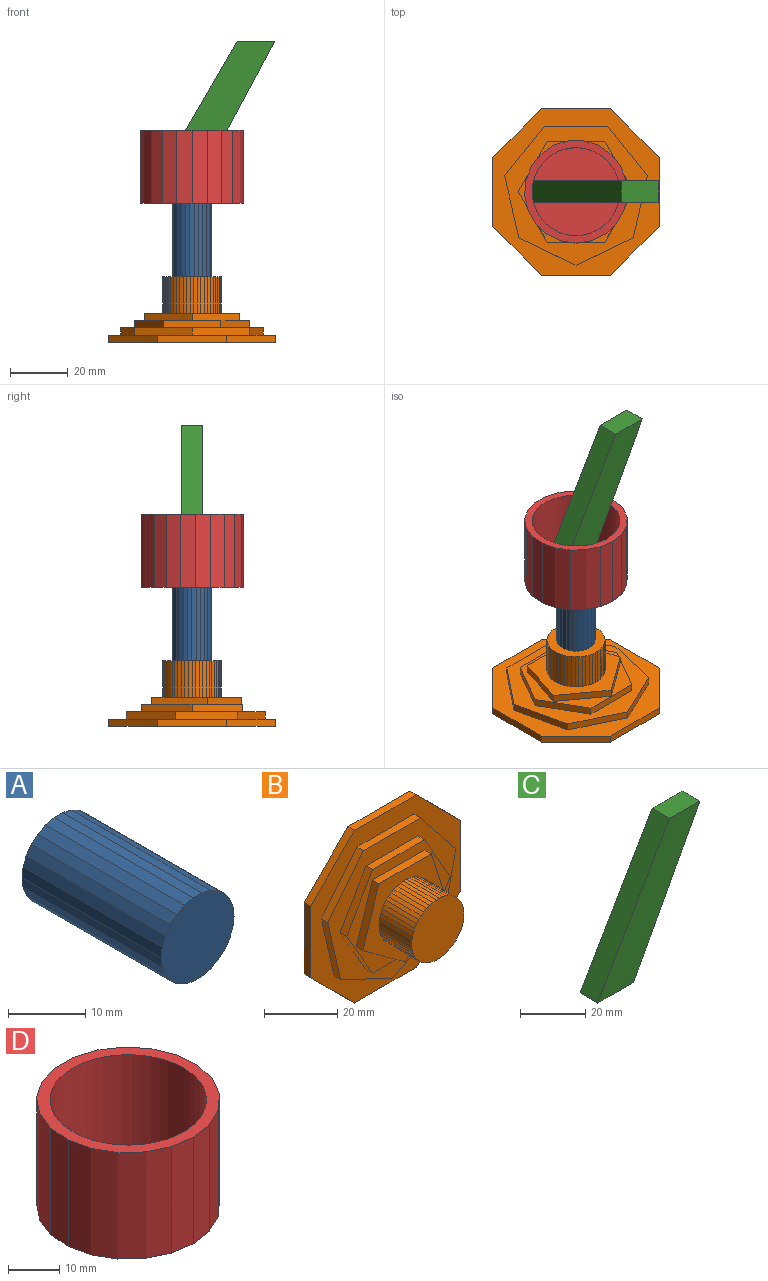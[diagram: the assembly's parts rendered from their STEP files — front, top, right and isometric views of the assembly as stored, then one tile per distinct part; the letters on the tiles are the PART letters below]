
ASSEMBLY  parts=4 mates=3
PART A: 28 faces, bbox 13.3x25.4x13.2 mm
  f0: plane 25.4x1.6mm, normal (0,0,-1), area 40.7mm2, adj f1,f25,f26,f27
  f1: plane 25.4x1.56mm, normal (0.24,0,-0.97), area 40.7mm2, adj f0,f2,f26,f27
  f2: plane 25.4x1.42mm, normal (0.46,0,-0.89), area 40.7mm2, adj f1,f3,f26,f27
  f3: plane 25.4x1.2mm, normal (0.66,0,-0.75), area 40.7mm2, adj f2,f4,f26,f27
  f4: plane 25.4x1.32mm, normal (0.82,0,-0.57), area 40.7mm2, adj f3,f5,f26,f27
  f5: plane 25.4x1.5mm, normal (0.94,0,-0.35), area 40.7mm2, adj f4,f6,f26,f27
  f6: plane 25.4x1.59mm, normal (0.99,0,-0.12), area 40.7mm2, adj f5,f7,f26,f27
  f7: plane 25.4x1.59mm, normal (0.99,0,0.12), area 40.7mm2, adj f6,f8,f26,f27
  f8: plane 25.4x1.5mm, normal (0.94,0,0.35), area 40.7mm2, adj f7,f9,f26,f27
  f9: plane 25.4x1.32mm, normal (0.82,0,0.57), area 40.7mm2, adj f8,f10,f26,f27
  f10: plane 25.4x1.2mm, normal (0.66,0,0.75), area 40.7mm2, adj f9,f11,f26,f27
  f11: plane 25.4x1.42mm, normal (0.46,0,0.89), area 40.7mm2, adj f10,f12,f26,f27
  f12: plane 25.4x1.56mm, normal (0.24,0,0.97), area 40.7mm2, adj f11,f13,f26,f27
  f13: plane 25.4x1.6mm, normal (0,0,1), area 40.7mm2, adj f12,f14,f26,f27
  f14: plane 25.4x1.56mm, normal (-0.24,0,0.97), area 40.7mm2, adj f13,f15,f26,f27
  f15: plane 25.4x1.42mm, normal (-0.46,0,0.89), area 40.7mm2, adj f14,f16,f26,f27
  f16: plane 25.4x1.2mm, normal (-0.66,0,0.75), area 40.7mm2, adj f15,f17,f26,f27
  f17: plane 25.4x1.32mm, normal (-0.82,0,0.57), area 40.7mm2, adj f16,f18,f26,f27
  f18: plane 25.4x1.5mm, normal (-0.94,0,0.35), area 40.7mm2, adj f17,f19,f26,f27
  f19: plane 25.4x1.59mm, normal (-0.99,0,0.12), area 40.7mm2, adj f18,f20,f26,f27
  f20: plane 25.4x1.59mm, normal (-0.99,0,-0.12), area 40.7mm2, adj f19,f21,f26,f27
  f21: plane 25.4x1.5mm, normal (-0.94,0,-0.35), area 40.7mm2, adj f20,f22,f26,f27
  f22: plane 25.4x1.32mm, normal (-0.82,0,-0.57), area 40.7mm2, adj f21,f23,f26,f27
  f23: plane 25.4x1.2mm, normal (-0.66,0,-0.75), area 40.7mm2, adj f22,f24,f26,f27
  f24: plane 25.4x1.42mm, normal (-0.46,0,-0.89), area 40.7mm2, adj f23,f25,f26,f27
  f25: plane 25.4x1.56mm, normal (-0.24,0,-0.97), area 40.7mm2, adj f0,f24,f26,f27
  f26: plane 13.3x13.2mm, normal (0,-1,0), area 137.6mm2, adj f0,f1,f2,f3,f4,f5,f6,f7
  f27: plane 13.3x13.2mm, normal (0,1,0), area 137.6mm2, adj f0,f1,f2,f3,f4,f5,f6,f7
PART B: 82 faces, bbox 57.8x22.9x57.8 mm
  f0: plane 40.1x34.73mm, normal (0,-1,0), area 341.7mm2, adj f19,f20,f21,f22,f23,f24,f25,f26
  f1: plane 49.54x48.29mm, normal (0,-1,0), area 721.6mm2, adj f12,f13,f14,f15,f16,f17,f18,f19
  f2: plane 57.82x57.82mm, normal (0,-1,0), area 1003.9mm2, adj f3,f4,f5,f6,f7,f8,f9,f10
  f3: plane 23.95x2.54mm, normal (0,0,1), area 60.8mm2, adj f2,f4,f10,f11
  f4: plane 16.94x16.94mm, normal (-0.71,0,0.71), area 60.8mm2, adj f2,f3,f5,f11
  f5: plane 23.95x2.54mm, normal (-1,0,0), area 60.8mm2, adj f2,f4,f6,f11
  f6: plane 16.94x16.94mm, normal (-0.71,0,-0.71), area 60.8mm2, adj f2,f5,f7,f11
  f7: plane 23.95x2.54mm, normal (0,0,-1), area 60.8mm2, adj f2,f6,f8,f11
  f8: plane 16.94x16.94mm, normal (0.71,0,-0.71), area 60.8mm2, adj f2,f7,f9,f11
  f9: plane 23.95x2.54mm, normal (1,0,0), area 60.8mm2, adj f2,f8,f10,f11
  f10: plane 16.94x16.94mm, normal (0.71,0,0.71), area 60.8mm2, adj f2,f3,f9,f11
  f11: plane 57.82x57.82mm, normal (0,1,0), area 2769.9mm2, adj f3,f4,f5,f6,f7,f8,f9,f10
  f12: plane 22.05x2.54mm, normal (0,0,1), area 56mm2, adj f1,f2,f13,f18
  f13: plane 17.24x13.75mm, normal (-0.78,0,0.62), area 56mm2, adj f1,f2,f12,f14
  f14: plane 21.49x4.91mm, normal (-0.97,0,-0.22), area 56mm2, adj f1,f2,f13,f15
  f15: plane 19.86x9.57mm, normal (-0.43,0,-0.9), area 56mm2, adj f1,f2,f14,f16
  f16: plane 19.86x9.57mm, normal (0.43,0,-0.9), area 56mm2, adj f1,f2,f15,f17
  f17: plane 21.49x4.91mm, normal (0.97,0,-0.22), area 56mm2, adj f1,f2,f16,f18
  f18: plane 17.24x13.75mm, normal (0.78,0,0.62), area 56mm2, adj f1,f2,f12,f17
  f19: plane 20.05x2.54mm, normal (0,0,1), area 50.9mm2, adj f0,f1,f20,f24
  f20: plane 17.36x10.03mm, normal (-0.87,0,0.5), area 50.9mm2, adj f0,f1,f19,f21
  f21: plane 17.36x10.03mm, normal (-0.87,0,-0.5), area 50.9mm2, adj f0,f1,f20,f22
  f22: plane 20.05x2.54mm, normal (0,0,-1), area 50.9mm2, adj f0,f1,f21,f23
  f23: plane 17.36x10.03mm, normal (0.87,0,-0.5), area 50.9mm2, adj f0,f1,f22,f24
  f24: plane 17.36x10.03mm, normal (0.87,0,0.5), area 50.9mm2, adj f0,f1,f19,f23
  f25: plane 20.21x2.54mm, normal (0,0,1), area 51.3mm2, adj f0,f26,f29,f30
  f26: plane 19.22x6.25mm, normal (-0.95,0,0.31), area 51.3mm2, adj f0,f25,f27,f30
  f27: plane 16.35x11.88mm, normal (-0.59,0,-0.81), area 51.3mm2, adj f0,f26,f28,f30
  f28: plane 16.35x11.88mm, normal (0.59,0,-0.81), area 51.3mm2, adj f0,f27,f29,f30
  f29: plane 19.22x6.25mm, normal (0.95,0,0.31), area 51.3mm2, adj f0,f25,f28,f30
  f30: plane 32.7x31.1mm, normal (0,-1,0), area 383.4mm2, adj f25,f26,f27,f28,f29,f31,f32,f33
  f31: plane 12.7x1.27mm, normal (0,0,-1), area 16.1mm2, adj f30,f32,f80,f81
  f32: plane 12.7x1.26mm, normal (0.13,0,-0.99), area 16.1mm2, adj f30,f31,f33,f81
  f33: plane 12.7x1.23mm, normal (0.25,0,-0.97), area 16.1mm2, adj f30,f32,f34,f81
  f34: plane 12.7x1.18mm, normal (0.37,0,-0.93), area 16.1mm2, adj f30,f33,f35,f81
  f35: plane 12.7x1.11mm, normal (0.48,0,-0.88), area 16.1mm2, adj f30,f34,f36,f81
  f36: plane 12.7x1.03mm, normal (0.59,0,-0.81), area 16.1mm2, adj f30,f35,f37,f81
  f37: plane 12.7x0.92mm, normal (0.68,0,-0.73), area 16.1mm2, adj f30,f36,f38,f81
  f38: plane 12.7x0.98mm, normal (0.77,0,-0.64), area 16.1mm2, adj f30,f37,f39,f81
  f39: plane 12.7x1.07mm, normal (0.84,0,-0.54), area 16.1mm2, adj f30,f38,f40,f81
  f40: plane 12.7x1.15mm, normal (0.9,0,-0.43), area 16.1mm2, adj f30,f39,f41,f81
  f41: plane 12.7x1.21mm, normal (0.95,0,-0.31), area 16.1mm2, adj f30,f40,f42,f81
  f42: plane 12.7x1.25mm, normal (0.98,0,-0.19), area 16.1mm2, adj f30,f41,f43,f81
  f43: plane 12.7x1.27mm, normal (1,0,-0.06), area 16.1mm2, adj f30,f42,f44,f81
  f44: plane 12.7x1.27mm, normal (1,0,0.06), area 16.1mm2, adj f30,f43,f45,f81
  f45: plane 12.7x1.25mm, normal (0.98,0,0.19), area 16.1mm2, adj f30,f44,f46,f81
  f46: plane 12.7x1.21mm, normal (0.95,0,0.31), area 16.1mm2, adj f30,f45,f47,f81
  f47: plane 12.7x1.15mm, normal (0.9,0,0.43), area 16.1mm2, adj f30,f46,f48,f81
  f48: plane 12.7x1.07mm, normal (0.84,0,0.54), area 16.1mm2, adj f30,f47,f49,f81
  f49: plane 12.7x0.98mm, normal (0.77,0,0.64), area 16.1mm2, adj f30,f48,f50,f81
  f50: plane 12.7x0.92mm, normal (0.68,0,0.73), area 16.1mm2, adj f30,f49,f51,f81
  f51: plane 12.7x1.03mm, normal (0.59,0,0.81), area 16.1mm2, adj f30,f50,f52,f81
  f52: plane 12.7x1.11mm, normal (0.48,0,0.88), area 16.1mm2, adj f30,f51,f53,f81
  f53: plane 12.7x1.18mm, normal (0.37,0,0.93), area 16.1mm2, adj f30,f52,f54,f81
  f54: plane 12.7x1.23mm, normal (0.25,0,0.97), area 16.1mm2, adj f30,f53,f55,f81
  f55: plane 12.7x1.26mm, normal (0.13,0,0.99), area 16.1mm2, adj f30,f54,f56,f81
  f56: plane 12.7x1.27mm, normal (0,0,1), area 16.1mm2, adj f30,f55,f57,f81
  f57: plane 12.7x1.26mm, normal (-0.13,0,0.99), area 16.1mm2, adj f30,f56,f58,f81
  f58: plane 12.7x1.23mm, normal (-0.25,0,0.97), area 16.1mm2, adj f30,f57,f59,f81
  f59: plane 12.7x1.18mm, normal (-0.37,0,0.93), area 16.1mm2, adj f30,f58,f60,f81
  f60: plane 12.7x1.11mm, normal (-0.48,0,0.88), area 16.1mm2, adj f30,f59,f61,f81
  f61: plane 12.7x1.03mm, normal (-0.59,0,0.81), area 16.1mm2, adj f30,f60,f62,f81
  f62: plane 12.7x0.92mm, normal (-0.68,0,0.73), area 16.1mm2, adj f30,f61,f63,f81
  f63: plane 12.7x0.98mm, normal (-0.77,0,0.64), area 16.1mm2, adj f30,f62,f64,f81
  f64: plane 12.7x1.07mm, normal (-0.84,0,0.54), area 16.1mm2, adj f30,f63,f65,f81
  f65: plane 12.7x1.15mm, normal (-0.9,0,0.43), area 16.1mm2, adj f30,f64,f66,f81
  f66: plane 12.7x1.21mm, normal (-0.95,0,0.31), area 16.1mm2, adj f30,f65,f67,f81
  f67: plane 12.7x1.25mm, normal (-0.98,0,0.19), area 16.1mm2, adj f30,f66,f68,f81
  f68: plane 12.7x1.27mm, normal (-1,0,0.06), area 16.1mm2, adj f30,f67,f69,f81
  f69: plane 12.7x1.27mm, normal (-1,0,-0.06), area 16.1mm2, adj f30,f68,f70,f81
  f70: plane 12.7x1.25mm, normal (-0.98,0,-0.19), area 16.1mm2, adj f30,f69,f71,f81
  f71: plane 12.7x1.21mm, normal (-0.95,0,-0.31), area 16.1mm2, adj f30,f70,f72,f81
  f72: plane 12.7x1.15mm, normal (-0.9,0,-0.43), area 16.1mm2, adj f30,f71,f73,f81
  f73: plane 12.7x1.07mm, normal (-0.84,0,-0.54), area 16.1mm2, adj f30,f72,f74,f81
  f74: plane 12.7x0.98mm, normal (-0.77,0,-0.64), area 16.1mm2, adj f30,f73,f75,f81
  f75: plane 12.7x0.92mm, normal (-0.68,0,-0.73), area 16.1mm2, adj f30,f74,f76,f81
  f76: plane 12.7x1.03mm, normal (-0.59,0,-0.81), area 16.1mm2, adj f30,f75,f77,f81
  f77: plane 12.7x1.11mm, normal (-0.48,0,-0.88), area 16.1mm2, adj f30,f76,f78,f81
  f78: plane 12.7x1.18mm, normal (-0.37,0,-0.93), area 16.1mm2, adj f30,f77,f79,f81
  f79: plane 12.7x1.23mm, normal (-0.25,0,-0.97), area 16.1mm2, adj f30,f78,f80,f81
  f80: plane 12.7x1.26mm, normal (-0.13,0,-0.99), area 16.1mm2, adj f30,f31,f79,f81
  f81: plane 20.19x20.15mm, normal (0,-1,0), area 319.4mm2, adj f31,f32,f33,f34,f35,f36,f37,f38
PART C: 6 faces, bbox 44.2x7.6x53.6 mm
  f0: plane 53.61x28.71mm, normal (0.88,0,-0.47), area 463.4mm2, adj f1,f3,f4,f5
  f1: plane 13.05x7.62mm, normal (0,0,1), area 99.4mm2, adj f0,f2,f4,f5
  f2: plane 53.61x31.12mm, normal (-0.86,0,0.5), area 472.3mm2, adj f1,f3,f4,f5
  f3: plane 15.46x7.62mm, normal (0,0,-1), area 117.8mm2, adj f0,f2,f4,f5
  f4: plane 53.61x44.17mm, normal (0,-1,0), area 764.2mm2, adj f0,f1,f2,f3
  f5: plane 53.61x44.17mm, normal (0,1,0), area 764.2mm2, adj f0,f1,f2,f3
PART D: 25 faces, bbox 35.6x35.5x25.4 mm
  f0: plane 25.4x5.33mm, normal (0,1,0), area 135.3mm2, adj f1,f20,f21,f22
  f1: plane 25.4x5.09mm, normal (-0.29,0.96,0), area 135.3mm2, adj f0,f2,f21,f22
  f2: plane 25.4x4.4mm, normal (-0.56,0.83,0), area 135.3mm2, adj f1,f3,f21,f22
  f3: plane 25.4x4.16mm, normal (-0.78,0.62,0), area 135.3mm2, adj f2,f4,f21,f22
  f4: plane 25.4x4.96mm, normal (-0.93,0.37,0), area 135.3mm2, adj f3,f5,f21,f22
  f5: plane 25.4x5.31mm, normal (-1,0.07,0), area 135.3mm2, adj f4,f6,f21,f22
  f6: plane 25.4x5.19mm, normal (-0.97,-0.22,0), area 135.3mm2, adj f5,f7,f21,f22
  f7: plane 25.4x4.61mm, normal (-0.87,-0.5,0), area 135.3mm2, adj f6,f8,f21,f22
  f8: plane 25.4x3.9mm, normal (-0.68,-0.73,0), area 135.3mm2, adj f7,f9,f21,f22
  f9: plane 25.4x4.8mm, normal (-0.43,-0.9,0), area 135.3mm2, adj f8,f10,f21,f22
  f10: plane 25.4x5.27mm, normal (-0.15,-0.99,0), area 135.3mm2, adj f9,f11,f21,f22
  f11: plane 25.4x5.27mm, normal (0.15,-0.99,0), area 135.3mm2, adj f10,f12,f21,f22
  f12: plane 25.4x4.8mm, normal (0.43,-0.9,0), area 135.3mm2, adj f11,f13,f21,f22
  f13: plane 25.4x3.9mm, normal (0.68,-0.73,0), area 135.3mm2, adj f12,f14,f21,f22
  f14: plane 25.4x4.61mm, normal (0.87,-0.5,0), area 135.3mm2, adj f13,f15,f21,f22
  f15: plane 25.4x5.19mm, normal (0.97,-0.22,0), area 135.3mm2, adj f14,f16,f21,f22
  f16: plane 25.4x5.31mm, normal (1,0.07,0), area 135.3mm2, adj f15,f17,f21,f22
  f17: plane 25.4x4.96mm, normal (0.93,0.37,0), area 135.3mm2, adj f16,f18,f21,f22
  f18: plane 25.4x4.16mm, normal (0.78,0.62,0), area 135.3mm2, adj f17,f19,f21,f22
  f19: plane 25.4x4.4mm, normal (0.56,0.83,0), area 135.3mm2, adj f18,f20,f21,f22
  f20: plane 25.4x5.09mm, normal (0.29,0.96,0), area 135.3mm2, adj f0,f19,f21,f22
  f21: plane 35.64x35.54mm, normal (0,0,1), area 258.4mm2, adj f0,f1,f2,f3,f4,f5,f6,f7
  f22: plane 35.64x35.54mm, normal (0,0,-1), area 988.1mm2, adj f0,f1,f2,f3,f4,f5,f6,f7
  f23: cylinder r=15.24mm len=30.48mm, axis (0,0,1), area 2189mm2, adj f21,f24
  f24: plane 30.48x30.48mm, normal (0,0,1), area 729.7mm2, adj f23
PLACE A rot(axis=(1,0,0),90deg) t=(163.57,52.78,136.42)mm
PLACE B rot(axis=(-1,0,0),90deg) t=(163.57,52.78,88.16)mm
PLACE C t=(142.29,56.59,138.96)mm
PLACE D t=(163.57,52.78,136.42)mm
MATE fastened B.f81 <-> A.f26  axis (0,0,1) through (163.57,52.78,111.02)mm
MATE fastened C.f3 <-> D.f23  axis (0,0,-1) through (163.57,52.78,138.96)mm
MATE fastened A.f27 <-> D.f23  axis (0,0,1) through (163.57,52.78,136.42)mm
